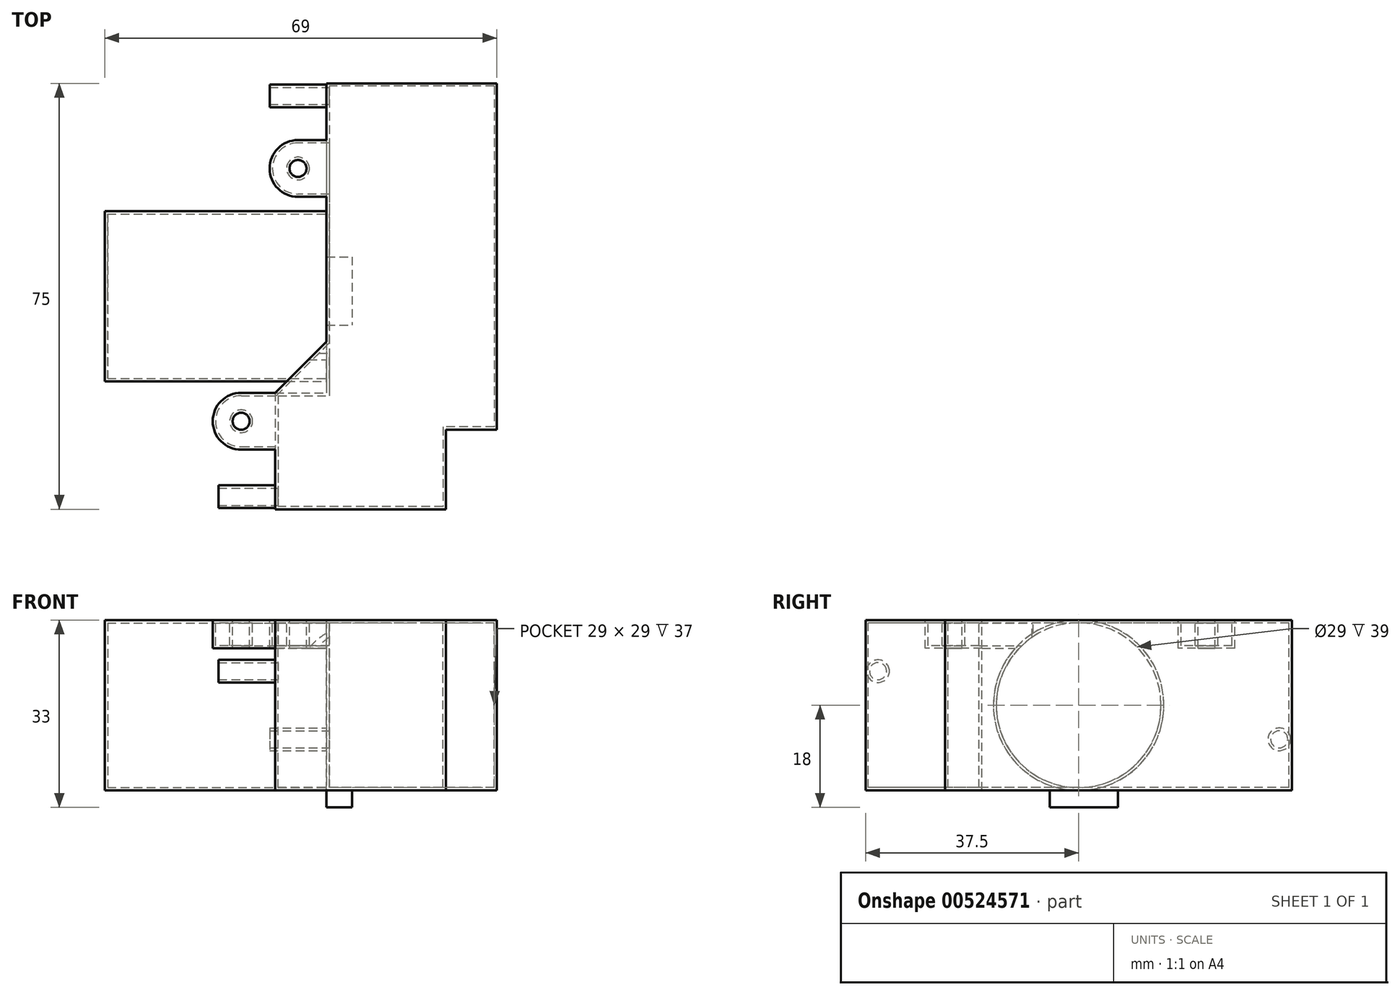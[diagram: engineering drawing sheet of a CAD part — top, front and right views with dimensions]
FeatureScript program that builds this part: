
annotation { "Feature Type Name" : "Feature", "Feature Type Description" : "" }
export const myFeature = defineFeature(function(context is Context, id is Id, definition is map)
    precondition{}
    {
        {
            var Q0;
            Q0=qCreatedBy(makeId("Top.planeOp"),FACE);
            var sketch = newSketch(context, id + "F0", { "sketchPlane" : qUnion([Q0])});
            skLineSegment(sketch, "E0.bottom", {"start": v(0, 0) * mm, "end": v(-30, 0) * mm});
            skLineSegment(sketch, "E0.top", {"start": v(0, -61) * mm, "end": v(-30, -61) * mm});
            skLineSegment(sketch, "E0.left", {"start": v(0, 0) * mm, "end": v(0, -61) * mm});
            skLineSegment(sketch, "E0.right", {"start": v(-30, 0) * mm, "end": v(-30, -61) * mm});
            skLineSegment(sketch, "E1", {"start": v(-8.65, 0) * mm, "end": v(-8.65, -10) * mm, "construction": true});
            skLineSegment(sketch, "E2", {"start": v(-45.93, -10) * mm, "end": v(0, -10) * mm, "construction": true});
            skLineSegment(sketch, "E3", {"start": v(-30, -15) * mm, "end": v(-35, -15) * mm, "construction": true});
            skLineSegment(sketch, "E4", {"start": v(-35, -15) * mm, "end": v(-35, -10) * mm, "construction": true});
            skCircle(sketch, "E5", {"center": v(-35, -15) * mm, "radius": 1.5 * mm});
            skLineSegment(sketch, "E6", {"start": v(-35, -15) * mm, "end": v(-59.35, -15) * mm, "construction": true});
            skCircle(sketch, "E7", {"center": v(-45, -59.5) * mm, "radius": 1.5 * mm});
            skLineSegment(sketch, "E8", {"start": v(0, -61) * mm, "end": v(-9, -61) * mm, "construction": true});
            skLineSegment(sketch, "E9.bottom", {"start": v(-9, -61) * mm, "end": v(-39, -61) * mm});
            skLineSegment(sketch, "E9.top", {"start": v(-9, -75) * mm, "end": v(-39, -75) * mm});
            skLineSegment(sketch, "E9.left", {"start": v(-9, -61) * mm, "end": v(-9, -75) * mm});
            skLineSegment(sketch, "E9.right", {"start": v(-39, -61) * mm, "end": v(-39, -75) * mm});
            skLineSegment(sketch, "E10.bottom", {"start": v(-45, -54.5) * mm, "end": v(-30, -54.5) * mm});
            skLineSegment(sketch, "E10.top", {"start": v(-45, -64.5) * mm, "end": v(-30, -64.5) * mm});
            skLineSegment(sketch, "E10.left", {"start": v(-45, -54.5) * mm, "end": v(-45, -64.5) * mm});
            skLineSegment(sketch, "E10.right", {"start": v(-30, -54.5) * mm, "end": v(-30, -64.5) * mm});
            skLineSegment(sketch, "E11", {"start": v(-30, -61) * mm, "end": v(-30, -64.5) * mm, "construction": true});
            skLineSegment(sketch, "E12", {"start": v(0, -61) * mm, "end": v(-2.48, -61) * mm, "construction": true});
            skLineSegment(sketch, "E13", {"start": v(-9, -61) * mm, "end": v(-62.74, -61) * mm, "construction": true});
            skLineSegment(sketch, "E14.bottom", {"start": v(-30, -10) * mm, "end": v(-35, -10) * mm});
            skLineSegment(sketch, "E14.top", {"start": v(-30, -20) * mm, "end": v(-35, -20) * mm});
            skLineSegment(sketch, "E14.left", {"start": v(-30, -10) * mm, "end": v(-30, -20) * mm});
            skLineSegment(sketch, "E14.right", {"start": v(-35, -10) * mm, "end": v(-35, -20) * mm});
            skCircle(sketch, "E15", {"center": v(-35, -15) * mm, "radius": 5 * mm});
            skPoint(sketch, "E15.third.point", {"position": v(-35, -20) * mm});
            skLineSegment(sketch, "E16", {"start": v(-30, -54.5) * mm, "end": v(-39, -54.5) * mm, "construction": true});
            skLineSegment(sketch, "E17", {"start": v(-39, -54.5) * mm, "end": v(-30, -45.5) * mm});
            skLineSegment(sketch, "E18", {"start": v(-45, -59.5) * mm, "end": v(0, -59.5) * mm, "construction": true});
            skCircle(sketch, "E19", {"center": v(-45, -59.5) * mm, "radius": 5 * mm});
            skLineSegment(sketch, "E20", {"start": v(-39, -54.5) * mm, "end": v(-39, -61) * mm});
            skSolve(sketch);
        }
        {
            var Q0;
            {var subQ1=sQuery(id+"F0.wireOp",EDGE,"E0.bottom");Q0=makeQuery(id+"F0.imprint","IMPRINT",FACE,{"disambiguationData":[TD([[makeQuery(id+"F0.imprint","IMPRINT",EDGE,{"derivedFrom":subQ1}),1.0]])]});}
            var Q1;
            {var subQ10=sQuery(id+"F0.wireOp",EDGE,"E10.left");Q1=makeQuery(id+"F0.imprint","IMPRINT",FACE,{"disambiguationData":[TD([[makeQuery(id+"F0.imprint","IMPRINT",EDGE,{"derivedFrom":subQ10}),1.0]])]});}
            var Q2;
            {var subQ3=sQuery(id+"F0.wireOp",EDGE,"E17");Q2=makeQuery(id+"F0.imprint","IMPRINT",FACE,{"disambiguationData":[TD([[makeQuery(id+"F0.imprint","IMPRINT",EDGE,{"derivedFrom":subQ3}),-1.0]])]});}
            var Q3;
            {var subQ0=sQuery(id+"F0.wireOp",EDGE,"E9.right");var subQ1=sQuery(id+"F0.wireOp",EDGE,"E9.bottom");var subQ2=makeQuery(id+"F0.imprint","INTERSECT",VERTEX,{"derivedFrom":[subQ1,subQ0]});Q3=makeQuery(id+"F0.imprint","IMPRINT",FACE,{"disambiguationData":[TD([[makeQuery(id+"F0.imprint","IMPRINT",EDGE,{"disambiguationData":[TD([[subQ2,1.0]])],"derivedFrom":subQ1}),1.0]])]});}
            var Q4;
            Q4=makeQuery(id+"F0.imprint","IMPRINT",FACE,{"disambiguationData":[TD([[makeQuery(id+"F0.imprint","IMPRINT",EDGE,{"derivedFrom":sQuery(id+"F0.wireOp",EDGE,"E7")}),-1.0]])]});
            var Q5;
            {var subQ0=sQuery(id+"F0.wireOp",EDGE,"E14.right");var subQ1=sQuery(id+"F0.wireOp",EDGE,"E5");var subQ2=makeQuery(id+"F0.imprint","INTERSECT",VERTEX,{"disambiguationData":[OD(0.0)],"derivedFrom":[subQ1,subQ0]});Q5=makeQuery(id+"F0.imprint","IMPRINT",FACE,{"disambiguationData":[TD([[makeQuery(id+"F0.imprint","IMPRINT",EDGE,{"disambiguationData":[TD([[subQ2,-1.0]])],"derivedFrom":subQ1}),-1.0]])]});}
            var Q6;
            {var subQ1=sQuery(id+"F0.wireOp",EDGE,"E14.right");var subQ5=sQuery(id+"F0.wireOp",EDGE,"E5");var subQ7=makeQuery(id+"F0.imprint","INTERSECT",VERTEX,{"disambiguationData":[OD(0.0)],"derivedFrom":[subQ5,subQ1]});Q6=makeQuery(id+"F0.imprint","IMPRINT",FACE,{"disambiguationData":[TD([[makeQuery(id+"F0.imprint","IMPRINT",EDGE,{"disambiguationData":[TD([[subQ7,1.0]])],"derivedFrom":subQ5}),-1.0]])]});}
            var Q7;
            {var subQ0=sQuery(id+"F0.wireOp",EDGE,"E14.top");Q7=makeQuery(id+"F0.imprint","IMPRINT",FACE,{"disambiguationData":[TD([[makeQuery(id+"F0.imprint","IMPRINT",EDGE,{"derivedFrom":subQ0}),-1.0]])]});}
            var Q8;
            {var subQ0=sQuery(id+"F0.wireOp",EDGE,"E14.bottom");Q8=makeQuery(id+"F0.imprint","IMPRINT",FACE,{"disambiguationData":[TD([[makeQuery(id+"F0.imprint","IMPRINT",EDGE,{"derivedFrom":subQ0}),1.0]])]});}
            var Q9;
            {var subQ0=sQuery(id+"F0.wireOp",EDGE,"E10.right");var subQ3=sQuery(id+"F0.wireOp",EDGE,"E9.bottom");var subQ4=makeQuery(id+"F0.imprint","INTERSECT",VERTEX,{"derivedFrom":[subQ3,subQ0]});Q9=makeQuery(id+"F0.imprint","IMPRINT",FACE,{"disambiguationData":[TD([[makeQuery(id+"F0.imprint","IMPRINT",EDGE,{"disambiguationData":[TD([[subQ4,-1.0]])],"derivedFrom":subQ3}),1.0]])]});}
            var Q10;
            {var subQ0=sQuery(id+"F0.wireOp",EDGE,"E10.right");var subQ4=sQuery(id+"F0.wireOp",EDGE,"E9.bottom");var subQ5=makeQuery(id+"F0.imprint","INTERSECT",VERTEX,{"derivedFrom":[subQ4,subQ0]});Q10=makeQuery(id+"F0.imprint","IMPRINT",FACE,{"disambiguationData":[TD([[makeQuery(id+"F0.imprint","IMPRINT",EDGE,{"disambiguationData":[TD([[subQ5,-1.0]])],"derivedFrom":subQ4}),-1.0]])]});}
            var Q11;
            {var subQ0=sQuery(id+"F0.wireOp",EDGE,"E10.top");var subQ1=sQuery(id+"F0.wireOp",EDGE,"E9.right");var subQ2=makeQuery(id+"F0.imprint","INTERSECT",VERTEX,{"derivedFrom":[subQ1,subQ0]});Q11=makeQuery(id+"F0.imprint","IMPRINT",FACE,{"disambiguationData":[TD([[makeQuery(id+"F0.imprint","IMPRINT",EDGE,{"disambiguationData":[TD([[subQ2,1.0]])],"derivedFrom":subQ1}),-1.0]])]});}
            extrude(context, id + "F1", {"entities" : qUnion([Q0, Q1, Q2, Q3, Q4, Q5, Q6, Q7, Q8, Q9, Q10, Q11]), "oppositeDirection" : true, "depth" : 5 * mm, "offsetDistance" : 25 * mm});
        }
        {
            var Q0;
            {var subQ1=sQuery(id+"F0.wireOp",EDGE,"E0.bottom");Q0=makeQuery(id+"F0.imprint","IMPRINT",FACE,{"disambiguationData":[TD([[makeQuery(id+"F0.imprint","IMPRINT",EDGE,{"derivedFrom":subQ1}),1.0]])]});}
            var Q1;
            {var subQ6=sQuery(id+"F0.wireOp",EDGE,"E9.top");Q1=makeQuery(id+"F0.imprint","IMPRINT",FACE,{"disambiguationData":[TD([[makeQuery(id+"F0.imprint","IMPRINT",EDGE,{"derivedFrom":subQ6}),-1.0]])]});}
            var Q2;
            {var subQ0=sQuery(id+"F0.wireOp",EDGE,"E20");Q2=makeQuery(id+"F0.imprint","IMPRINT",FACE,{"disambiguationData":[TD([[makeQuery(id+"F0.imprint","IMPRINT",EDGE,{"derivedFrom":subQ0}),1.0]])]});}
            var Q3;
            {var subQ3=sQuery(id+"F0.wireOp",EDGE,"E10.right");var subQ5=sQuery(id+"F0.wireOp",EDGE,"E10.top");var subQ7=makeQuery(id+"F0.imprint","INTERSECT",VERTEX,{"derivedFrom":[subQ5,subQ3]});Q3=makeQuery(id+"F0.imprint","IMPRINT",FACE,{"disambiguationData":[TD([[makeQuery(id+"F0.imprint","IMPRINT",EDGE,{"disambiguationData":[TD([[subQ7,1.0]])],"derivedFrom":subQ5}),1.0]])]});}
            extrude(context, id + "F2", {"entities" : qUnion([Q0, Q1, Q2, Q3]), "oppositeDirection" : true, "depth" : 30 * mm, "offsetDistance" : 25 * mm});
        }
        {
            var Q0;
            Q0=makeQuery(id+"F2.opExtrude","SWEPT_FACE",FACE,{"disambiguationData":[OSD([sQuery(id+"F0.wireOp",EDGE,"E0.right"),sQuery(id+"F0.wireOp",EDGE,"E14.left")])]});
            var sketch = newSketch(context, id + "F3", { "sketchPlane" : qUnion([Q0])});
            skLineSegment(sketch, "E21", {"start": v(0, -15) * mm, "end": v(0, -30) * mm, "construction": true});
            skLineSegment(sketch, "E22", {"start": v(0, -15) * mm, "end": v(37.5, -15) * mm, "construction": true});
            skCircle(sketch, "E23", {"center": v(37.5, -15) * mm, "radius": 15 * mm});
            skSolve(sketch);
        }
        {
            var Q0;
            Q0 = qSketchRegion(id + "F3", true);
            extrude(context, id + "F4", {"entities" : qUnion([Q0]), "operationType" : NewBodyOperationType.ADD, "depth" : 39 * mm, "offsetDistance" : 25 * mm});
        }
        {
            var Q0;
            Q0=makeQuery(id+"F2.opExtrude","SWEPT_FACE",FACE,{"disambiguationData":[OSD([sQuery(id+"F0.wireOp",EDGE,"E9.right"),sQuery(id+"F0.wireOp",EDGE,"E20")])]});
            var sketch = newSketch(context, id + "F5", { "sketchPlane" : qUnion([Q0])});
            skLineSegment(sketch, "E24", {"start": v(72.8, 0) * mm, "end": v(72.8, -9) * mm, "construction": true});
            skLineSegment(sketch, "E25", {"start": v(75, -7.14) * mm, "end": v(72.8, -7.14) * mm, "construction": true});
            skCircle(sketch, "E26", {"center": v(72.8, -9) * mm, "radius": 2 * mm});
            skSolve(sketch);
        }
        {
            var Q0;
            {var subQ1=sQuery(id+"F0.wireOp",EDGE,"E14.left");var subQ6=sQuery(id+"F0.wireOp",EDGE,"E0.right");var subQ9=sQuery(id+"F0.wireOp",EDGE,"E0.bottom");var subQ10=makeQuery(id+"F2.opExtrude","SWEPT_FACE",FACE,{"disambiguationData":[OSD([subQ6,subQ1])]});Q0=makeQuery(id+"F4.boolean.opBoolean","SPLIT",FACE,{"disambiguationData":[TD([makeQuery(id+"F2.opExtrude","SWEPT_FACE",FACE,{"disambiguationData":[OSD([subQ9])]})])],"derivedFrom":subQ10});}
            var sketch = newSketch(context, id + "F6", { "sketchPlane" : qUnion([Q0])});
            skLineSegment(sketch, "E27", {"start": v(2.2, -30) * mm, "end": v(2.2, -21) * mm, "construction": true});
            skLineSegment(sketch, "E28", {"start": v(2.2, -21) * mm, "end": v(0, -21) * mm, "construction": true});
            skCircle(sketch, "E29", {"center": v(2.2, -21) * mm, "radius": 2 * mm});
            skSolve(sketch);
        }
        {
            var Q0;
            Q0=makeQuery(id+"F5.imprint","IMPRINT",FACE,{"disambiguationData":[TD([[makeQuery(id+"F5.imprint","IMPRINT",EDGE,{"derivedFrom":sQuery(id+"F5.wireOp",EDGE,"E26")}),1.0]])]});
            var Q1;
            Q1=makeQuery(id+"F6.imprint","IMPRINT",FACE,{"disambiguationData":[TD([[makeQuery(id+"F6.imprint","IMPRINT",EDGE,{"derivedFrom":sQuery(id+"F6.wireOp",EDGE,"E29")}),1.0]])]});
            extrude(context, id + "F7", {"entities" : qUnion([Q0, Q1]), "operationType" : NewBodyOperationType.ADD, "depth" : 10 * mm, "offsetDistance" : 25 * mm});
        }
        {
            var Q0;
            Q0=makeQuery(id+"F7.opExtrude","CAP_FACE",FACE,{"disambiguationData":[OSD([sQuery(id+"F5.wireOp",EDGE,"E26")])],"isStart":false});
            var Q1;
            Q1=makeQuery(id+"F7.opExtrude","CAP_FACE",FACE,{"disambiguationData":[OSD([sQuery(id+"F6.wireOp",EDGE,"E29")])],"isStart":false});
            shell(context, id + "F8", {"entities" : qUnion([Q0, Q1]), "thickness" : 0.5 * mm});
        }
        {
            var Q0;
            Q0=makeQuery(id+"F2.opExtrude","CAP_FACE",FACE,{"disambiguationData":[OSD([sQuery(id+"F0.wireOp",EDGE,"E0.bottom"),sQuery(id+"F0.wireOp",EDGE,"E0.top"),sQuery(id+"F0.wireOp",EDGE,"E0.left"),sQuery(id+"F0.wireOp",EDGE,"E0.right"),sQuery(id+"F0.wireOp",EDGE,"E9.top"),sQuery(id+"F0.wireOp",EDGE,"E9.left"),sQuery(id+"F0.wireOp",EDGE,"E9.right"),sQuery(id+"F0.wireOp",EDGE,"E10.bottom"),sQuery(id+"F0.wireOp",EDGE,"E14.left"),sQuery(id+"F0.wireOp",EDGE,"E20")])],"isStart":false});
            var sketch = newSketch(context, id + "F9", { "sketchPlane" : qUnion([Q0])});
            skLineSegment(sketch, "E30.bottom", {"start": v(-30, 30.57) * mm, "end": v(-25.5, 30.57) * mm});
            skLineSegment(sketch, "E30.top", {"start": v(-30, 42.57) * mm, "end": v(-25.5, 42.57) * mm});
            skLineSegment(sketch, "E30.left", {"start": v(-30, 30.57) * mm, "end": v(-30, 42.57) * mm});
            skLineSegment(sketch, "E30.right", {"start": v(-25.5, 30.57) * mm, "end": v(-25.5, 42.57) * mm});
            skSolve(sketch);
        }
        {
            var Q0;
            Q0 = qSketchRegion(id + "F9", true);
            extrude(context, id + "F10", {"entities" : qUnion([Q0]), "operationType" : NewBodyOperationType.ADD, "depth" : 3 * mm, "offsetDistance" : 25 * mm});
        }
    });
